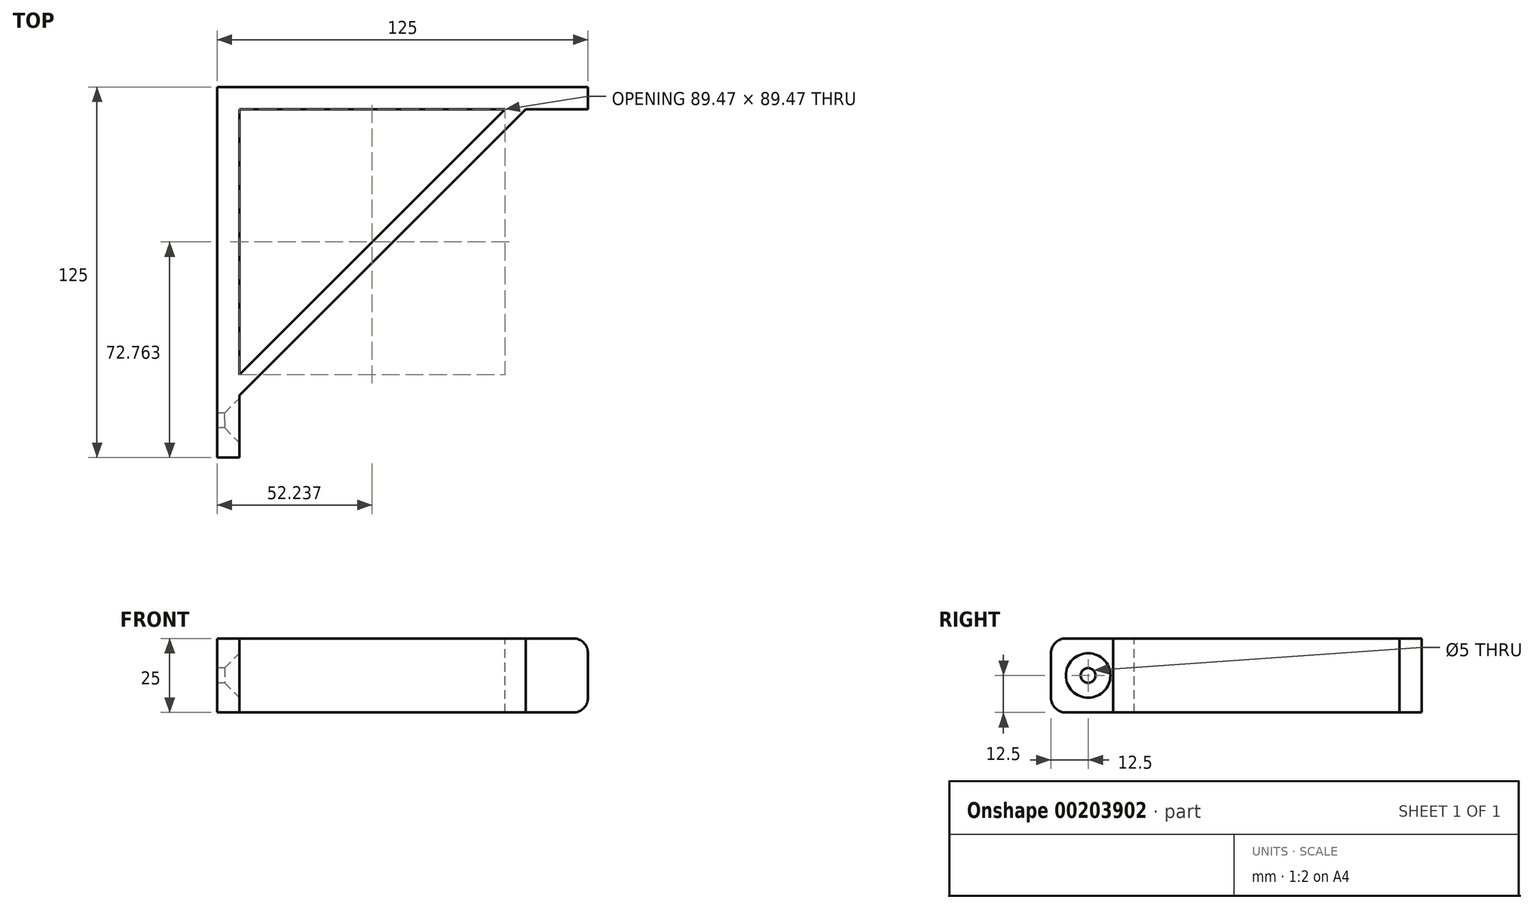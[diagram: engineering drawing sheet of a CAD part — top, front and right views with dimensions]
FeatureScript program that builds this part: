
annotation { "Feature Type Name" : "Feature", "Feature Type Description" : "" }
export const myFeature = defineFeature(function(context is Context, id is Id, definition is map)
    precondition{}
    {
        {
            var Q0;
            Q0=qCreatedBy(makeId("Top.planeOp"),FACE);
            var sketch = newSketch(context, id + "F0", { "sketchPlane" : qUnion([Q0])});
            skLineSegment(sketch, "E0", {"start": v(0, 0) * mm, "end": v(0, -125) * mm});
            skLineSegment(sketch, "E1", {"start": v(0, 0) * mm, "end": v(125, 0) * mm});
            skLineSegment(sketch, "E2.0", {"start": v(7.5, 0) * mm, "end": v(7.5, -125) * mm});
            skLineSegment(sketch, "E3.0", {"start": v(0, -7.5) * mm, "end": v(125, -7.5) * mm});
            skLineSegment(sketch, "E4", {"start": v(125, 0) * mm, "end": v(125, -7.5) * mm});
            skLineSegment(sketch, "E5", {"start": v(7.5, -125) * mm, "end": v(0, -125) * mm});
            skSolve(sketch);
        }
        {
            var Q0;
            {var subQ0=sQuery(id+"F0.wireOp",EDGE,"E4");Q0=makeQuery(id+"F0.imprint","IMPRINT",FACE,{"disambiguationData":[TD([[makeQuery(id+"F0.imprint","IMPRINT",EDGE,{"derivedFrom":subQ0}),-1.0]])]});}
            var Q1;
            {var subQ0=sQuery(id+"F0.wireOp",EDGE,"E1");var subQ1=sQuery(id+"F0.wireOp",EDGE,"E0");var subQ2=makeQuery(id+"F0.imprint","INTERSECT",VERTEX,{"derivedFrom":[subQ1,subQ0]});Q1=makeQuery(id+"F0.imprint","IMPRINT",FACE,{"disambiguationData":[TD([[makeQuery(id+"F0.imprint","IMPRINT",EDGE,{"disambiguationData":[TD([[subQ2,-1.0]])],"derivedFrom":subQ1}),1.0]])]});}
            var Q2;
            {var subQ0=sQuery(id+"F0.wireOp",EDGE,"E5");Q2=makeQuery(id+"F0.imprint","IMPRINT",FACE,{"disambiguationData":[TD([[makeQuery(id+"F0.imprint","IMPRINT",EDGE,{"derivedFrom":subQ0}),-1.0]])]});}
            extrude(context, id + "F1", {"entities" : qUnion([Q0, Q1, Q2]), "depth" : 25 * mm});
        }
        {
            var Q0;
            Q0=makeQuery(id+"F1.opExtrude","CAP_FACE",FACE,{"disambiguationData":[OSD([sQuery(id+"F0.wireOp",EDGE,"E0"),sQuery(id+"F0.wireOp",EDGE,"E1"),sQuery(id+"F0.wireOp",EDGE,"E2.0"),sQuery(id+"F0.wireOp",EDGE,"E3.0"),sQuery(id+"F0.wireOp",EDGE,"E4"),sQuery(id+"F0.wireOp",EDGE,"E5")])],"isStart":false});
            var sketch = newSketch(context, id + "F2", { "sketchPlane" : qUnion([Q0])});
            skLineSegment(sketch, "E6", {"start": v(0, 0) * mm, "end": v(7.5, -7.5) * mm, "construction": true});
            skLineSegment(sketch, "E7", {"start": v(0, 0) * mm, "end": v(103.17, -103.17) * mm, "construction": true});
            skLineSegment(sketch, "E8", {"start": v(7.5, -96.97) * mm, "end": v(96.97, -7.5) * mm});
            skLineSegment(sketch, "E9.0", {"start": v(11.04, -100.5) * mm, "end": v(100.5, -11.04) * mm});
            skLineSegment(sketch, "E10", {"start": v(11.04, -100.5) * mm, "end": v(7.5, -104.04) * mm});
            skLineSegment(sketch, "E11", {"start": v(7.5, -104.04) * mm, "end": v(104.04, -7.5) * mm});
            skSolve(sketch);
        }
        {
            var Q0;
            {var subQ0=sQuery(id+"F2.wireOp",EDGE,"E8");Q0=makeQuery(id+"F2.imprint","IMPRINT",FACE,{"disambiguationData":[TD([[makeQuery(id+"F2.imprint","IMPRINT",EDGE,{"derivedFrom":subQ0}),-1.0]])]});}
            extrude(context, id + "F3", {"entities" : qUnion([Q0]), "operationType" : NewBodyOperationType.ADD, "oppositeDirection" : true, "depth" : 25 * mm});
        }
        {
            var Q0;
            Q0=makeQuery(id+"F1.opExtrude","SWEPT_FACE",FACE,{"disambiguationData":[OSD([sQuery(id+"F0.wireOp",EDGE,"E0")])]});
            var sketch = newSketch(context, id + "F4", { "sketchPlane" : qUnion([Q0])});
            skCircle(sketch, "E12", {"center": v(112.5, 12.5) * mm, "radius": 2.5 * mm});
            skPoint(sketch, "E12.centerSnap0", {"position": v(125, 12.5) * mm});
            skSolve(sketch);
        }
        {
            var Q0;
            Q0=makeQuery(id+"F4.imprint","IMPRINT",FACE,{"disambiguationData":[TD([[makeQuery(id+"F4.imprint","IMPRINT",EDGE,{"derivedFrom":sQuery(id+"F4.wireOp",EDGE,"E12")}),1.0]])]});
            extrude(context, id + "F5", {"entities" : qUnion([Q0]), "operationType" : NewBodyOperationType.REMOVE, "oppositeDirection" : true, "depth" : 25 * mm});
        }
        {
            var Q0;
            {var subQ0=sQuery(id+"F0.wireOp",EDGE,"E5");var subQ4=sQuery(id+"F0.wireOp",EDGE,"E2.0");Q0=makeQuery(id+"F5.boolean.opBoolean","INTERSECT",EDGE,{"derivedFrom":[makeQuery(id+"F3.boolean.opBoolean","SPLIT",FACE,{"disambiguationData":[TD([makeQuery(id+"F1.opExtrude","SWEPT_FACE",FACE,{"disambiguationData":[OSD([subQ0])]})])],"derivedFrom":makeQuery(id+"F1.opExtrude","SWEPT_FACE",FACE,{"disambiguationData":[OSD([subQ4])]})}),makeQuery(id+"F5.opExtrude","SWEPT_FACE",FACE,{"disambiguationData":[OSD([sQuery(id+"F4.wireOp",EDGE,"E12")])]})]});}
            chamfer(context, id + "F6", {"entities" : qUnion([Q0]), "width" : 5 * mm, "tangentPropagation" : true});
        }
        {
            var Q0;
            Q0=makeQuery(id+"F1.opExtrude","CAP_EDGE",EDGE,{"disambiguationData":[OSD([sQuery(id+"F0.wireOp",EDGE,"E5")])],"isStart":false});
            var Q1;
            Q1=makeQuery(id+"F1.opExtrude","CAP_EDGE",EDGE,{"disambiguationData":[OSD([sQuery(id+"F0.wireOp",EDGE,"E5")])],"isStart":true});
            var Q2;
            Q2=makeQuery(id+"F1.opExtrude","CAP_EDGE",EDGE,{"disambiguationData":[OSD([sQuery(id+"F0.wireOp",EDGE,"E4")])],"isStart":false});
            var Q3;
            Q3=makeQuery(id+"F1.opExtrude","CAP_EDGE",EDGE,{"disambiguationData":[OSD([sQuery(id+"F0.wireOp",EDGE,"E4")])],"isStart":true});
            fillet(context, id + "F7", {"entities" : qUnion([Q0, Q1, Q2, Q3]), "radius" : 5 * mm, "tangentPropagation" : true, "allowEdgeOverflow" : false});
        }
    });
